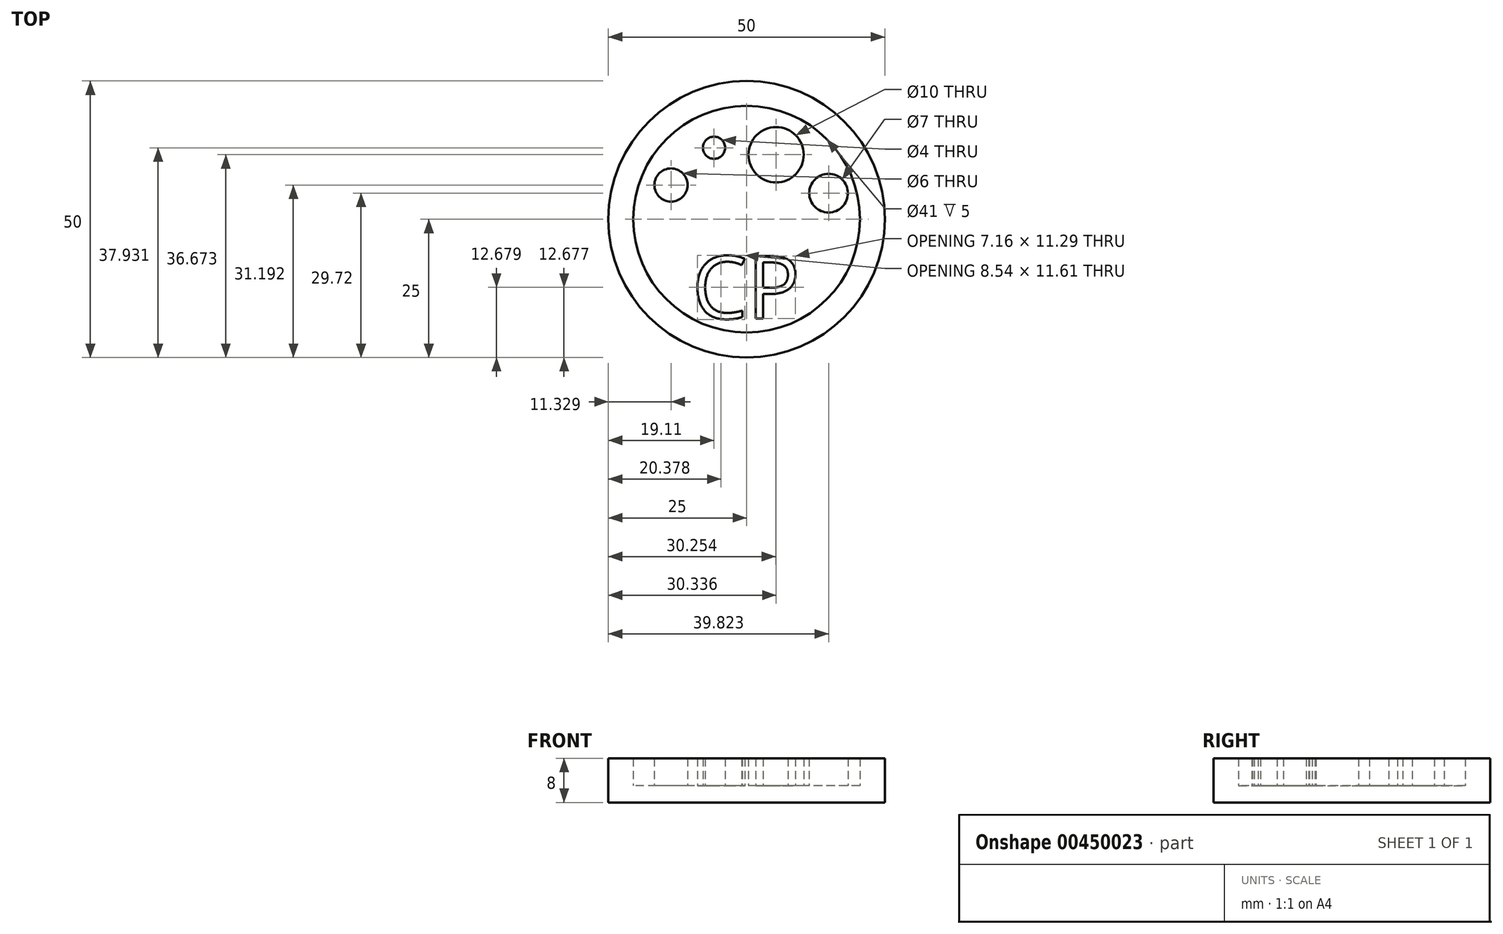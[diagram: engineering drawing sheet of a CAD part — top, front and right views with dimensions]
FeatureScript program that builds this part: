
annotation { "Feature Type Name" : "Feature", "Feature Type Description" : "" }
export const myFeature = defineFeature(function(context is Context, id is Id, definition is map)
    precondition{}
    {
        {
            var Q0;
            Q0=qCreatedBy(makeId("Top.planeOp"),FACE);
            var sketch = newSketch(context, id + "F0", { "sketchPlane" : qUnion([Q0])});
            skCircle(sketch, "E0", {"center": v(0, 0) * mm, "radius": 20.5 * mm});
            skCircle(sketch, "E1", {"center": v(0, 0) * mm, "radius": 25 * mm});
            skText(sketch, "E2", { "text": "CP", "fontName": "OpenSans-Regular.ttf"});
            skCircle(sketch, "E3", {"center": v(5.34, 11.67) * mm, "radius": 5 * mm});
            skCircle(sketch, "E4", {"center": v(14.82, 4.72) * mm, "radius": 3.5 * mm});
            skCircle(sketch, "E5", {"center": v(-5.89, 12.93) * mm, "radius": 2 * mm});
            skCircle(sketch, "E6", {"center": v(-13.67, 6.2) * mm, "radius": 3 * mm});
            const initialGuessF0  = {"E2": [-0.00986, -0.01797, 1, 0, 0.01139]};
            skSetInitialGuess(sketch, initialGuessF0);
            skSolve(sketch);
        }
        {
            var Q0;
            Q0=makeQuery(id+"F0.imprint","IMPRINT",FACE,{"disambiguationData":[TD([[makeQuery(id+"F0.imprint","IMPRINT",EDGE,{"derivedFrom":sQuery(id+"F0.wireOp",EDGE,"E0")}),-1.0]])]});
            extrude(context, id + "F1", {"entities" : qUnion([Q0]), "depth" : 8 * mm});
        }
        {
            var Q0;
            Q0=makeQuery(id+"F0.imprint","IMPRINT",FACE,{"disambiguationData":[TD([[makeQuery(id+"F0.imprint","IMPRINT",EDGE,{"derivedFrom":sQuery(id+"F0.wireOp",EDGE,"E0")}),1.0]])]});
            extrude(context, id + "F2", {"entities" : qUnion([Q0]), "operationType" : NewBodyOperationType.ADD, "depth" : 3 * mm});
        }
        {
            var Q0;
            Q0=makeQuery(id+"F0.imprint","IMPRINT",FACE,{"disambiguationData":[TD([[makeQuery(id+"F0.imprint","IMPRINT",EDGE,{"derivedFrom":sQuery(id+"F0.wireOp",EDGE,"E2.sketch_text.stroke-0")}),-1.0]])]});
            var Q1;
            Q1=makeQuery(id+"F0.imprint","IMPRINT",FACE,{"disambiguationData":[TD([[makeQuery(id+"F0.imprint","IMPRINT",EDGE,{"derivedFrom":sQuery(id+"F0.wireOp",EDGE,"E2.sketch_text.stroke-15")}),-1.0]])]});
            var Q2;
            Q2=makeQuery(id+"F0.imprint","IMPRINT",FACE,{"disambiguationData":[TD([[makeQuery(id+"F0.imprint","IMPRINT",EDGE,{"derivedFrom":sQuery(id+"F0.wireOp",EDGE,"E6")}),1.0]])]});
            var Q3;
            Q3=makeQuery(id+"F0.imprint","IMPRINT",FACE,{"disambiguationData":[TD([[makeQuery(id+"F0.imprint","IMPRINT",EDGE,{"derivedFrom":sQuery(id+"F0.wireOp",EDGE,"E5")}),1.0]])]});
            var Q4;
            Q4=makeQuery(id+"F0.imprint","IMPRINT",FACE,{"disambiguationData":[TD([[makeQuery(id+"F0.imprint","IMPRINT",EDGE,{"derivedFrom":sQuery(id+"F0.wireOp",EDGE,"E3")}),1.0]])]});
            var Q5;
            Q5=makeQuery(id+"F0.imprint","IMPRINT",FACE,{"disambiguationData":[TD([[makeQuery(id+"F0.imprint","IMPRINT",EDGE,{"derivedFrom":sQuery(id+"F0.wireOp",EDGE,"E4")}),1.0]])]});
            extrude(context, id + "F3", {"entities" : qUnion([Q0, Q1, Q2, Q3, Q4, Q5]), "operationType" : NewBodyOperationType.ADD, "depth" : 8 * mm});
        }
        {
            var Q0;
            Q0=makeQuery(id+"F0.imprint","IMPRINT",FACE,{"disambiguationData":[TD([[makeQuery(id+"F0.imprint","IMPRINT",EDGE,{"derivedFrom":sQuery(id+"F0.wireOp",EDGE,"E2.sketch_text.stroke-23")}),1.0]])]});
            extrude(context, id + "F4", {"entities" : qUnion([Q0]), "operationType" : NewBodyOperationType.ADD, "depth" : 3 * mm});
        }
        {
            var Q0;
            Q0=makeQuery(id+"F2.opExtrude","CAP_FACE",FACE,{"disambiguationData":[OSD([sQuery(id+"F0.wireOp",EDGE,"E0"),sQuery(id+"F0.wireOp",EDGE,"E2.sketch_text.stroke-0"),sQuery(id+"F0.wireOp",EDGE,"E2.sketch_text.stroke-1"),sQuery(id+"F0.wireOp",EDGE,"E2.sketch_text.stroke-2"),sQuery(id+"F0.wireOp",EDGE,"E2.sketch_text.stroke-3"),sQuery(id+"F0.wireOp",EDGE,"E2.sketch_text.stroke-4"),sQuery(id+"F0.wireOp",EDGE,"E2.sketch_text.stroke-5"),sQuery(id+"F0.wireOp",EDGE,"E2.sketch_text.stroke-6"),sQuery(id+"F0.wireOp",EDGE,"E2.sketch_text.stroke-7"),sQuery(id+"F0.wireOp",EDGE,"E2.sketch_text.stroke-8"),sQuery(id+"F0.wireOp",EDGE,"E2.sketch_text.stroke-9"),sQuery(id+"F0.wireOp",EDGE,"E2.sketch_text.stroke-10"),sQuery(id+"F0.wireOp",EDGE,"E2.sketch_text.stroke-11"),sQuery(id+"F0.wireOp",EDGE,"E2.sketch_text.stroke-12"),sQuery(id+"F0.wireOp",EDGE,"E2.sketch_text.stroke-13"),sQuery(id+"F0.wireOp",EDGE,"E2.sketch_text.stroke-14"),sQuery(id+"F0.wireOp",EDGE,"E2.sketch_text.stroke-15"),sQuery(id+"F0.wireOp",EDGE,"E2.sketch_text.stroke-16"),sQuery(id+"F0.wireOp",EDGE,"E2.sketch_text.stroke-17"),sQuery(id+"F0.wireOp",EDGE,"E2.sketch_text.stroke-18"),sQuery(id+"F0.wireOp",EDGE,"E2.sketch_text.stroke-19"),sQuery(id+"F0.wireOp",EDGE,"E2.sketch_text.stroke-20"),sQuery(id+"F0.wireOp",EDGE,"E2.sketch_text.stroke-21"),sQuery(id+"F0.wireOp",EDGE,"E2.sketch_text.stroke-22"),sQuery(id+"F0.wireOp",EDGE,"E3"),sQuery(id+"F0.wireOp",EDGE,"E4"),sQuery(id+"F0.wireOp",EDGE,"E5"),sQuery(id+"F0.wireOp",EDGE,"E6")])],"isStart":false});
            extrude(context, id + "F5", {"entities" : qUnion([Q0]), "depth" : 5 * mm});
        }
    });
